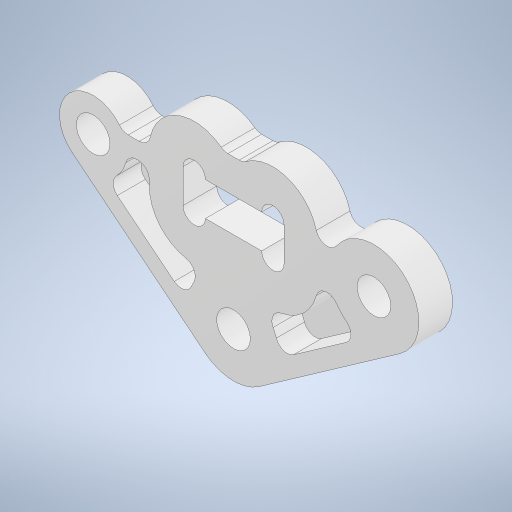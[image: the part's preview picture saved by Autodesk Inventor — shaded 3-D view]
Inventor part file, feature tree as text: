
AUTODESK INVENTOR PART (.ipt)
format: ipt  version: 2023.1 (Build 271208000, 208)  size: 559,104 bytes
history: native  units: mm
features: extrude x7, sketch x5, other x4, fillet x3, hole x1
ambient origin geometry x8: Origin, YZ Plane, XZ Plane, XY Plane, X Axis, Y Axis, Z Axis, Center Point
bodies: Body1 (feature_tree)
feature tree (20):
  extrude  "押し出し2"  Depth=1.5mm
  hole  "穴1"  [1 undecoded]
  fillet  "フィレット1"  Radius=3.0mm
  sketch  "スケッチ3"
  extrude  "押し出し3"  Depth=3.0mm TaperAngle=0.0deg
  extrude  "押し出し4"  Depth=1.0mm
  extrude  "押し出し5"  Depth=9.0mm
  extrude  "押し出し6"  Depth=3.0mm
  fillet  "フィレット2"  Radius=2.0mm
  extrude  "押し出し7"  Depth=2.0mm
  extrude  "押し出し8"  Depth=2.0mm
  fillet  "フィレット3"  Radius=2.0mm
  sketch  "スケッチ1"
  sketch  "スケッチ2"
  sketch  "スケッチ4"
  sketch  "スケッチ5"
  other  "断面エッジを投影1"
  other  "断面エッジを投影2"
  other  "断面エッジを投影3"
  other  "断面エッジを投影4"
note: 1 required parameter value undecoded (feature->parameter linkage not recoverable at this tier; creation-order binding heuristic only, values carry confidence <= 0.55)
